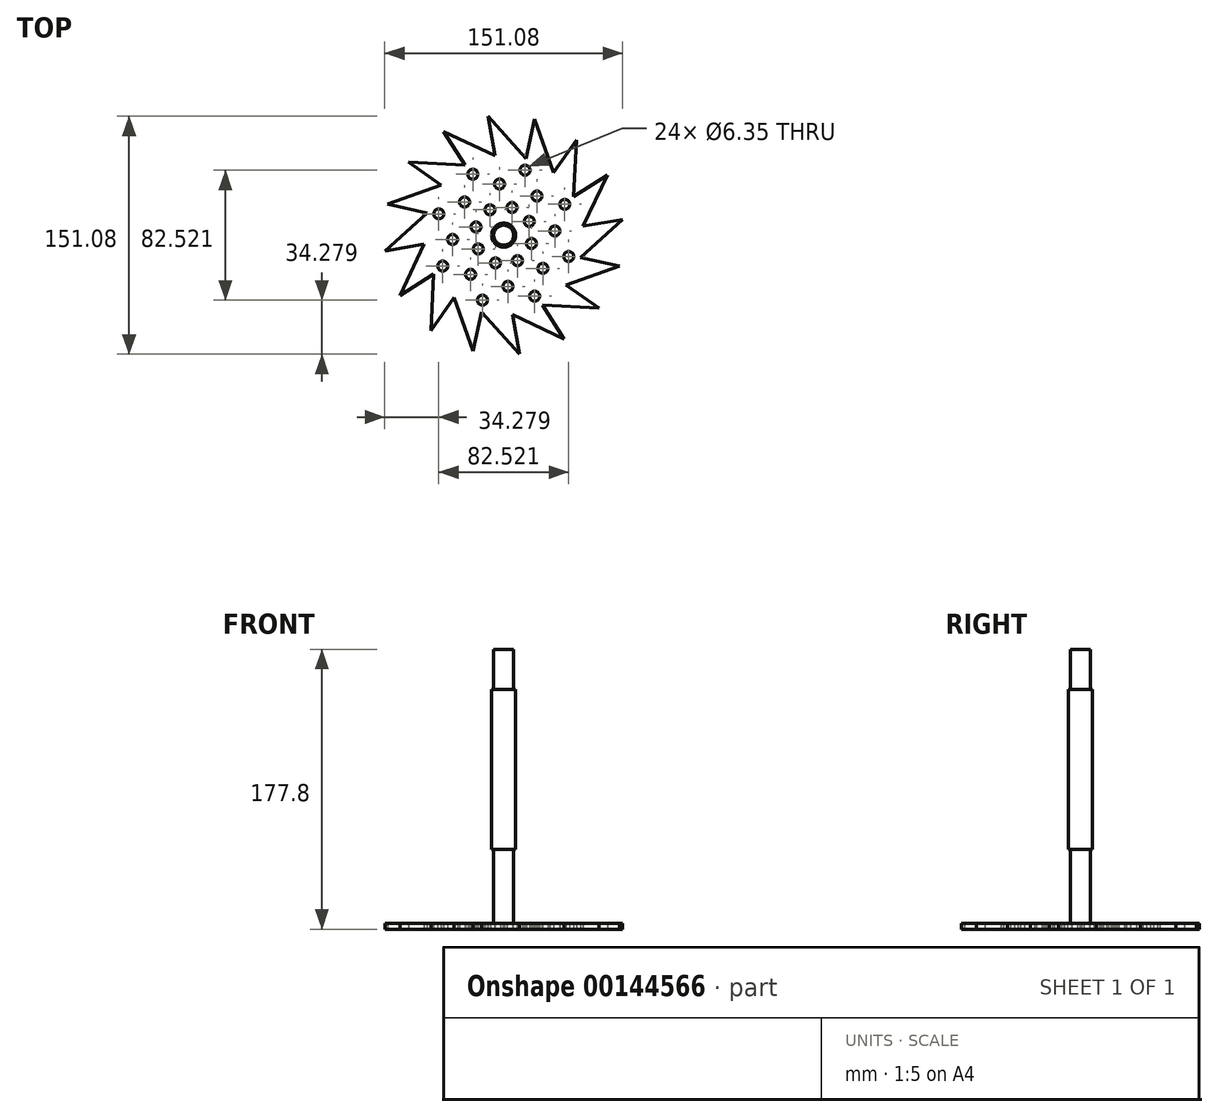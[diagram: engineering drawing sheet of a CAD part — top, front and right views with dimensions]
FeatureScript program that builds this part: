
annotation { "Feature Type Name" : "Feature", "Feature Type Description" : "" }
export const myFeature = defineFeature(function(context is Context, id is Id, definition is map)
    precondition{}
    {
        {
            var Q0;
            Q0=qCreatedBy(makeId("Front.planeOp"),FACE);
            var sketch = newSketch(context, id + "F0", { "sketchPlane" : qUnion([Q0])});
            skLineSegment(sketch, "E0", {"start": v(0, 0) * mm, "end": v(0, 177.8) * mm});
            skSolve(sketch);
        }
        {
            var Q0;
            Q0=qCreatedBy(makeId("Top.planeOp"),FACE);
            cPlane(context, id + "F1", {"entities" : qUnion([Q0]), "cplaneType" : CPlaneType.OFFSET, "offset" : 177.8 * mm, "width" : 152.4 * mm, "height" : 152.4 * mm});
        }
        {
            var Q0;
            Q0=sQuery(id+"F0.wireOp",EDGE,"E0");
            cPlane(context, id + "F2", {"entities" : qUnion([Q0]), "cplaneType" : CPlaneType.LINE_ANGLE, "offset" : 25.4 * mm, "angle" : 45 * degree, "width" : 152.4 * mm, "height" : 152.4 * mm});
        }
        {
            var Q0;
            Q0=sQuery(id+"F0.wireOp",EDGE,"E0");
            cPlane(context, id + "F3", {"entities" : qUnion([Q0]), "cplaneType" : CPlaneType.LINE_ANGLE, "offset" : 25.4 * mm, "angle" : 135 * degree, "width" : 152.4 * mm, "height" : 152.4 * mm});
        }
        {
            var Q0;
            Q0=qCreatedBy(id+"F1.planeOp",FACE);
            var sketch = newSketch(context, id + "F4", { "sketchPlane" : qUnion([Q0])});
            skCircle(sketch, "E1", {"center": v(0, 0) * mm, "radius": 6.35 * mm});
            skSolve(sketch);
        }
        {
            var Q0;
            Q0=makeQuery(id+"F4.imprint","IMPRINT",FACE,{"disambiguationData":[TD([[makeQuery(id+"F4.imprint","IMPRINT",EDGE,{"derivedFrom":sQuery(id+"F4.wireOp",EDGE,"E1")}),1.0]])]});
            extrude(context, id + "F5", {"entities" : qUnion([Q0]), "oppositeDirection" : true, "depth" : 177.8 * mm});
        }
        {
            var Q0;
            Q0=qCreatedBy(makeId("Top.planeOp"),FACE);
            var sketch = newSketch(context, id + "F6", { "sketchPlane" : qUnion([Q0])});
            skCircle(sketch, "E2", {"center": v(0, 0) * mm, "radius": 76.2 * mm});
            skCircle(sketch, "E3", {"center": v(0, 0) * mm, "radius": 50.8 * mm});
            skLineSegment(sketch, "E4", {"start": v(48.8, -14.08) * mm, "end": v(73.63, -19.64) * mm});
            skLineSegment(sketch, "E5.1.0", {"start": v(50.48, 5.67) * mm, "end": v(75.54, 10.03) * mm});
            skLineSegment(sketch, "E5.2.0", {"start": v(44.47, 24.56) * mm, "end": v(65.95, 38.18) * mm});
            skLineSegment(sketch, "E6.1.3.0", {"start": v(31.69, 39.7) * mm, "end": v(46.32, 60.5) * mm});
            skLineSegment(sketch, "E6.1.4.0", {"start": v(14.08, 48.8) * mm, "end": v(19.64, 73.63) * mm});
            skLineSegment(sketch, "E6.1.5.0", {"start": v(-5.67, 50.48) * mm, "end": v(-10.03, 75.54) * mm});
            skLineSegment(sketch, "E6.1.6.0", {"start": v(-24.56, 44.47) * mm, "end": v(-38.18, 65.95) * mm});
            skLineSegment(sketch, "E6.1.7.0", {"start": v(-39.7, 31.69) * mm, "end": v(-60.5, 46.32) * mm});
            skLineSegment(sketch, "E6.1.8.0", {"start": v(-48.8, 14.08) * mm, "end": v(-73.63, 19.64) * mm});
            skLineSegment(sketch, "E6.1.9.0", {"start": v(-50.48, -5.67) * mm, "end": v(-75.54, -10.03) * mm});
            skLineSegment(sketch, "E6.1.10.0", {"start": v(-44.47, -24.56) * mm, "end": v(-65.95, -38.18) * mm});
            skLineSegment(sketch, "E6.1.11.0", {"start": v(-31.69, -39.7) * mm, "end": v(-46.32, -60.5) * mm});
            skLineSegment(sketch, "E6.1.12.0", {"start": v(-14.08, -48.8) * mm, "end": v(-19.64, -73.63) * mm});
            skLineSegment(sketch, "E6.1.13.0", {"start": v(5.67, -50.48) * mm, "end": v(10.03, -75.54) * mm});
            skLineSegment(sketch, "E6.1.14.0", {"start": v(24.56, -44.47) * mm, "end": v(38.18, -65.95) * mm});
            skLineSegment(sketch, "E6.1.15.0", {"start": v(39.7, -31.69) * mm, "end": v(60.5, -46.32) * mm});
            skLineSegment(sketch, "E7", {"start": v(48.8, -14.08) * mm, "end": v(75.54, 10.03) * mm});
            skLineSegment(sketch, "E8.1.0", {"start": v(50.48, 5.67) * mm, "end": v(65.95, 38.18) * mm});
            skLineSegment(sketch, "E8.2.0", {"start": v(44.47, 24.56) * mm, "end": v(46.32, 60.5) * mm});
            skLineSegment(sketch, "E9.1.3.0", {"start": v(31.69, 39.7) * mm, "end": v(19.64, 73.63) * mm});
            skLineSegment(sketch, "E9.1.4.0", {"start": v(14.08, 48.8) * mm, "end": v(-10.03, 75.54) * mm});
            skLineSegment(sketch, "E9.1.5.0", {"start": v(-5.67, 50.48) * mm, "end": v(-38.18, 65.95) * mm});
            skLineSegment(sketch, "E9.1.6.0", {"start": v(-24.56, 44.47) * mm, "end": v(-60.5, 46.32) * mm});
            skLineSegment(sketch, "E9.1.7.0", {"start": v(-39.7, 31.69) * mm, "end": v(-73.63, 19.64) * mm});
            skLineSegment(sketch, "E9.1.8.0", {"start": v(-48.8, 14.08) * mm, "end": v(-75.54, -10.03) * mm});
            skLineSegment(sketch, "E9.1.9.0", {"start": v(-50.48, -5.67) * mm, "end": v(-65.95, -38.18) * mm});
            skLineSegment(sketch, "E9.1.10.0", {"start": v(-44.47, -24.56) * mm, "end": v(-46.32, -60.5) * mm});
            skLineSegment(sketch, "E9.1.11.0", {"start": v(-31.69, -39.7) * mm, "end": v(-19.64, -73.63) * mm});
            skLineSegment(sketch, "E9.1.12.0", {"start": v(-14.08, -48.8) * mm, "end": v(10.03, -75.54) * mm});
            skLineSegment(sketch, "E9.1.13.0", {"start": v(5.67, -50.48) * mm, "end": v(38.18, -65.95) * mm});
            skLineSegment(sketch, "E9.1.14.0", {"start": v(24.56, -44.47) * mm, "end": v(60.5, -46.32) * mm});
            skLineSegment(sketch, "E9.1.15.0", {"start": v(39.7, -31.69) * mm, "end": v(73.63, -19.64) * mm});
            skCircle(sketch, "E10", {"center": v(41.26, -13.53) * mm, "radius": 3.18 * mm});
            skCircle(sketch, "E11.1.0", {"center": v(38.74, 19.61) * mm, "radius": 3.18 * mm});
            skCircle(sketch, "E11.2.0", {"center": v(13.53, 41.26) * mm, "radius": 3.18 * mm});
            skCircle(sketch, "E12.1.3.0", {"center": v(-19.61, 38.74) * mm, "radius": 3.18 * mm});
            skCircle(sketch, "E12.1.4.0", {"center": v(-41.26, 13.53) * mm, "radius": 3.18 * mm});
            skCircle(sketch, "E12.1.5.0", {"center": v(-38.74, -19.61) * mm, "radius": 3.18 * mm});
            skCircle(sketch, "E12.1.6.0", {"center": v(-13.53, -41.26) * mm, "radius": 3.18 * mm});
            skCircle(sketch, "E12.1.7.0", {"center": v(19.61, -38.74) * mm, "radius": 3.18 * mm});
            skCircle(sketch, "E13", {"center": v(-2.69, 32.5) * mm, "radius": 3.18 * mm});
            skCircle(sketch, "E14.1.0", {"center": v(-24.88, 21.08) * mm, "radius": 3.18 * mm});
            skCircle(sketch, "E14.2.0", {"center": v(-32.5, -2.69) * mm, "radius": 3.18 * mm});
            skCircle(sketch, "E15.1.3.0", {"center": v(-21.08, -24.88) * mm, "radius": 3.18 * mm});
            skCircle(sketch, "E15.1.4.0", {"center": v(2.69, -32.5) * mm, "radius": 3.18 * mm});
            skCircle(sketch, "E15.1.5.0", {"center": v(24.88, -21.08) * mm, "radius": 3.18 * mm});
            skCircle(sketch, "E15.1.6.0", {"center": v(32.5, 2.69) * mm, "radius": 3.18 * mm});
            skCircle(sketch, "E15.1.7.0", {"center": v(21.08, 24.88) * mm, "radius": 3.18 * mm});
            skCircle(sketch, "E16", {"center": v(16.17, 8.74) * mm, "radius": 3.18 * mm});
            skCircle(sketch, "E17.1.0", {"center": v(5.25, 17.61) * mm, "radius": 3.18 * mm});
            skCircle(sketch, "E17.2.0", {"center": v(-8.74, 16.17) * mm, "radius": 3.18 * mm});
            skCircle(sketch, "E18.1.3.0", {"center": v(-17.61, 5.25) * mm, "radius": 3.18 * mm});
            skCircle(sketch, "E18.1.4.0", {"center": v(-16.17, -8.74) * mm, "radius": 3.18 * mm});
            skCircle(sketch, "E18.1.5.0", {"center": v(-5.25, -17.61) * mm, "radius": 3.18 * mm});
            skCircle(sketch, "E18.1.6.0", {"center": v(8.74, -16.17) * mm, "radius": 3.18 * mm});
            skCircle(sketch, "E18.1.7.0", {"center": v(17.61, -5.25) * mm, "radius": 3.18 * mm});
            skSolve(sketch);
        }
        {
            var Q0;
            {var subQ2=sQuery(id+"F6.wireOp",EDGE,"E6.1.3.0");Q0=makeQuery(id+"F6.imprint","IMPRINT",FACE,{"disambiguationData":[TD([[makeQuery(id+"F6.imprint","IMPRINT",EDGE,{"derivedFrom":subQ2}),-1.0]])]});}
            var Q1;
            {var subQ2=sQuery(id+"F6.wireOp",EDGE,"E6.1.4.0");Q1=makeQuery(id+"F6.imprint","IMPRINT",FACE,{"disambiguationData":[TD([[makeQuery(id+"F6.imprint","IMPRINT",EDGE,{"derivedFrom":subQ2}),-1.0]])]});}
            var Q2;
            {var subQ2=sQuery(id+"F6.wireOp",EDGE,"E6.1.5.0");Q2=makeQuery(id+"F6.imprint","IMPRINT",FACE,{"disambiguationData":[TD([[makeQuery(id+"F6.imprint","IMPRINT",EDGE,{"derivedFrom":subQ2}),-1.0]])]});}
            var Q3;
            {var subQ2=sQuery(id+"F6.wireOp",EDGE,"E6.1.6.0");Q3=makeQuery(id+"F6.imprint","IMPRINT",FACE,{"disambiguationData":[TD([[makeQuery(id+"F6.imprint","IMPRINT",EDGE,{"derivedFrom":subQ2}),-1.0]])]});}
            var Q4;
            {var subQ2=sQuery(id+"F6.wireOp",EDGE,"E6.1.7.0");Q4=makeQuery(id+"F6.imprint","IMPRINT",FACE,{"disambiguationData":[TD([[makeQuery(id+"F6.imprint","IMPRINT",EDGE,{"derivedFrom":subQ2}),-1.0]])]});}
            var Q5;
            {var subQ2=sQuery(id+"F6.wireOp",EDGE,"E6.1.8.0");Q5=makeQuery(id+"F6.imprint","IMPRINT",FACE,{"disambiguationData":[TD([[makeQuery(id+"F6.imprint","IMPRINT",EDGE,{"derivedFrom":subQ2}),-1.0]])]});}
            var Q6;
            {var subQ2=sQuery(id+"F6.wireOp",EDGE,"E6.1.9.0");Q6=makeQuery(id+"F6.imprint","IMPRINT",FACE,{"disambiguationData":[TD([[makeQuery(id+"F6.imprint","IMPRINT",EDGE,{"derivedFrom":subQ2}),-1.0]])]});}
            var Q7;
            {var subQ2=sQuery(id+"F6.wireOp",EDGE,"E6.1.10.0");Q7=makeQuery(id+"F6.imprint","IMPRINT",FACE,{"disambiguationData":[TD([[makeQuery(id+"F6.imprint","IMPRINT",EDGE,{"derivedFrom":subQ2}),-1.0]])]});}
            var Q8;
            {var subQ2=sQuery(id+"F6.wireOp",EDGE,"E6.1.11.0");Q8=makeQuery(id+"F6.imprint","IMPRINT",FACE,{"disambiguationData":[TD([[makeQuery(id+"F6.imprint","IMPRINT",EDGE,{"derivedFrom":subQ2}),-1.0]])]});}
            var Q9;
            {var subQ2=sQuery(id+"F6.wireOp",EDGE,"E5.2.0");Q9=makeQuery(id+"F6.imprint","IMPRINT",FACE,{"disambiguationData":[TD([[makeQuery(id+"F6.imprint","IMPRINT",EDGE,{"derivedFrom":subQ2}),-1.0]])]});}
            var Q10;
            {var subQ0=sQuery(id+"F6.wireOp",EDGE,"E4");Q10=makeQuery(id+"F6.imprint","IMPRINT",FACE,{"disambiguationData":[TD([[makeQuery(id+"F6.imprint","IMPRINT",EDGE,{"derivedFrom":subQ0}),-1.0]])]});}
            var Q11;
            {var subQ2=sQuery(id+"F6.wireOp",EDGE,"E6.1.15.0");Q11=makeQuery(id+"F6.imprint","IMPRINT",FACE,{"disambiguationData":[TD([[makeQuery(id+"F6.imprint","IMPRINT",EDGE,{"derivedFrom":subQ2}),-1.0]])]});}
            var Q12;
            {var subQ2=sQuery(id+"F6.wireOp",EDGE,"E6.1.14.0");Q12=makeQuery(id+"F6.imprint","IMPRINT",FACE,{"disambiguationData":[TD([[makeQuery(id+"F6.imprint","IMPRINT",EDGE,{"derivedFrom":subQ2}),-1.0]])]});}
            var Q13;
            {var subQ2=sQuery(id+"F6.wireOp",EDGE,"E6.1.12.0");Q13=makeQuery(id+"F6.imprint","IMPRINT",FACE,{"disambiguationData":[TD([[makeQuery(id+"F6.imprint","IMPRINT",EDGE,{"derivedFrom":subQ2}),-1.0]])]});}
            var Q14;
            {var subQ2=sQuery(id+"F6.wireOp",EDGE,"E5.1.0");Q14=makeQuery(id+"F6.imprint","IMPRINT",FACE,{"disambiguationData":[TD([[makeQuery(id+"F6.imprint","IMPRINT",EDGE,{"derivedFrom":subQ2}),-1.0]])]});}
            var Q15;
            Q15=makeQuery(id+"F6.imprint","IMPRINT",FACE,{"disambiguationData":[TD([[makeQuery(id+"F6.imprint","IMPRINT",EDGE,{"derivedFrom":sQuery(id+"F6.wireOp",EDGE,"E10")}),-1.0]])]});
            var Q16;
            {var subQ2=sQuery(id+"F6.wireOp",EDGE,"E6.1.13.0");Q16=makeQuery(id+"F6.imprint","IMPRINT",FACE,{"disambiguationData":[TD([[makeQuery(id+"F6.imprint","IMPRINT",EDGE,{"derivedFrom":subQ2}),-1.0]])]});}
            extrude(context, id + "F7", {"entities" : qUnion([Q0, Q1, Q2, Q3, Q4, Q5, Q6, Q7, Q8, Q9, Q10, Q11, Q12, Q13, Q14, Q15, Q16]), "operationType" : NewBodyOperationType.ADD, "depth" : 3.8 * mm});
        }
        {
            var Q0;
            Q0=qCreatedBy(makeId("Top.planeOp"),FACE);
            cPlane(context, id + "F8", {"entities" : qUnion([Q0]), "cplaneType" : CPlaneType.OFFSET, "offset" : 101.6 * mm, "width" : 152.4 * mm, "height" : 152.4 * mm});
        }
        {
            var Q0;
            Q0=qCreatedBy(id+"F8.planeOp",FACE);
            var sketch = newSketch(context, id + "F9", { "sketchPlane" : qUnion([Q0])});
            skCircle(sketch, "E19", {"center": v(0, 0) * mm, "radius": 7.62 * mm});
            skSolve(sketch);
        }
        {
            var Q0;
            Q0 = qSketchRegion(id + "F9", true);
            extrude(context, id + "F10", {"entities" : qUnion([Q0]), "operationType" : NewBodyOperationType.ADD, "endBound" : BoundingType.SYMMETRIC, "depth" : 101.6 * mm});
        }
    });
